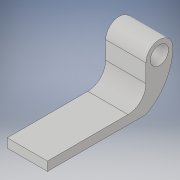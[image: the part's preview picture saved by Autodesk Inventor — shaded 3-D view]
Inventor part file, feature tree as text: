
AUTODESK INVENTOR PART (.ipt)
format: ipt  version: 2017 (Build 210142000, 142)  size: 116,736 bytes
history: native  units: in
note: dims shown in document units (in); Inventor stores cm internally (conversion verified against a paired STEP export)
features: sketch x2, extrude x1, fillet x1, hole x1, projected_geometry x1
ambient origin geometry x8: Origin, YZ Plane, XZ Plane, XY Plane, X Axis, Y Axis, Z Axis, Center Point
bodies: Solid1 (feature_tree)
feature tree (6):
  extrude  "Extrusion1"  Depth=2.75in
  fillet  "Fillet1"  Radius=2.75in
  hole  "Hole1"  [1 undecoded]
  sketch  "Sketch1"  dims[d0=0.75in d4=1.0in d5=2.75in]
  sketch  "Sketch2"  dims[d6=0.25in d7=1.125in d8=0.0in d9=0.5in d10=0.505in d11=0.75in d12=0.375in d13=0.25in d14=0.5635in d15=1.0in d16=0.8108in]
  projected_geometry  "Projected Loop1"
note: 1 required parameter value undecoded (feature->parameter linkage not recoverable at this tier; creation-order binding heuristic only, values carry confidence <= 0.55)
